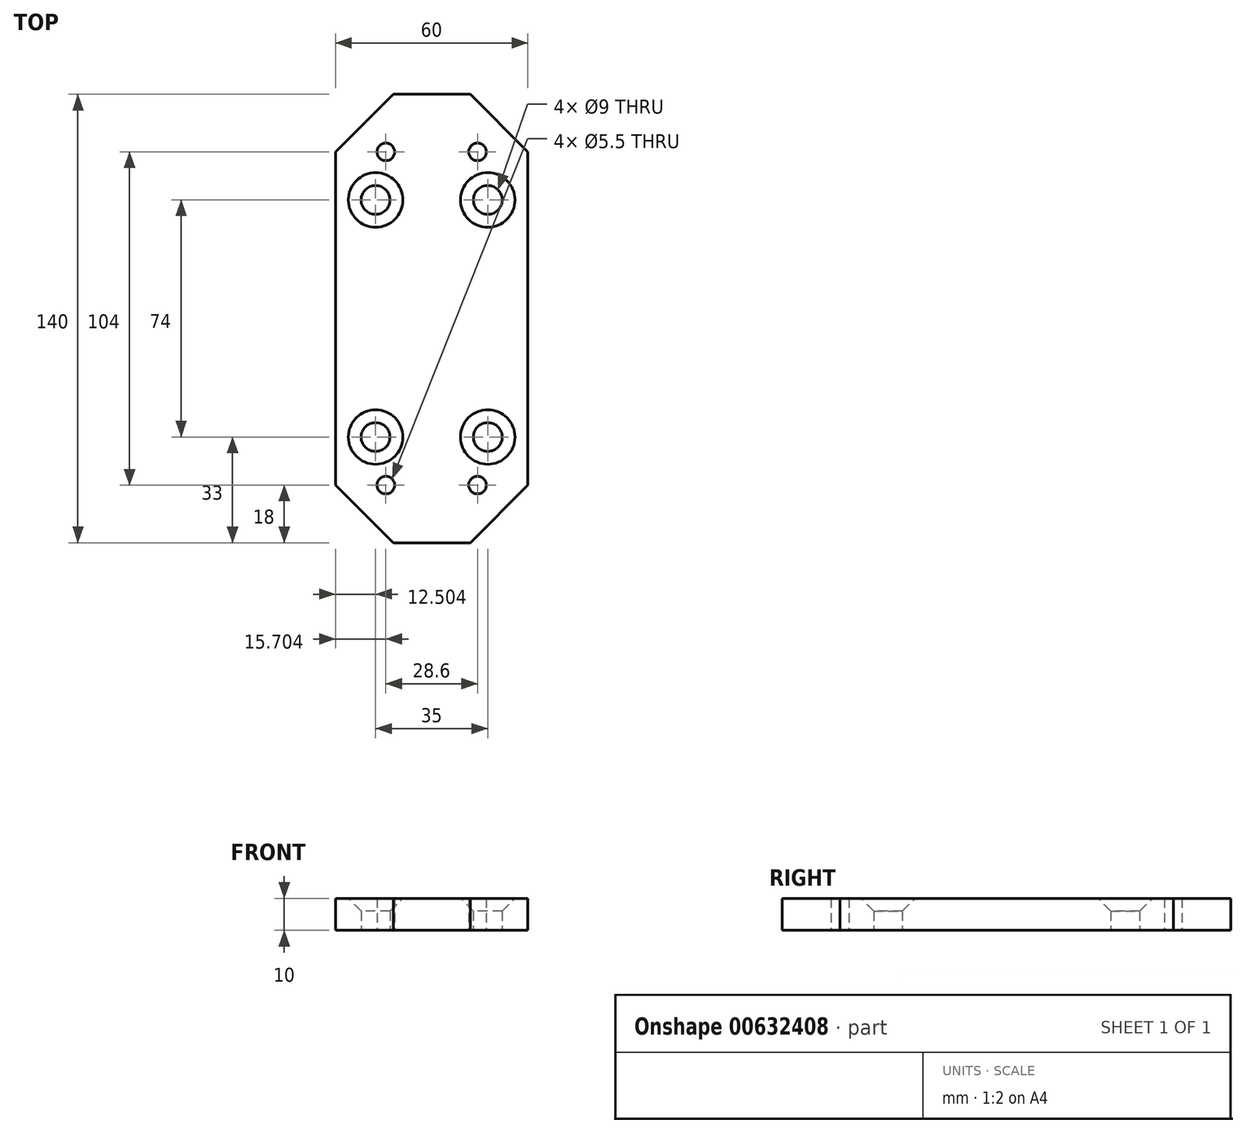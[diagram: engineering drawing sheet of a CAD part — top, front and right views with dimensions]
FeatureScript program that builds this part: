
annotation { "Feature Type Name" : "Feature", "Feature Type Description" : "" }
export const myFeature = defineFeature(function(context is Context, id is Id, definition is map)
    precondition{}
    {
        {
            var Q0;
            Q0=qCreatedBy(makeId("Top.planeOp"),FACE);
            var sketch = newSketch(context, id + "F0", { "sketchPlane" : qUnion([Q0])});
            skLineSegment(sketch, "E0.bottom", {"start": v(27.22, 0) * mm, "end": v(-32.78, 0) * mm});
            skLineSegment(sketch, "E0.top", {"start": v(27.22, 140) * mm, "end": v(-32.78, 140) * mm});
            skLineSegment(sketch, "E0.left", {"start": v(27.22, 0) * mm, "end": v(27.22, 140) * mm});
            skLineSegment(sketch, "E0.right", {"start": v(-32.78, 0) * mm, "end": v(-32.78, 140) * mm});
            skCircle(sketch, "E1", {"center": v(-20.28, 33) * mm, "radius": 4.5 * mm});
            skCircle(sketch, "E2", {"center": v(14.72, 33) * mm, "radius": 4.5 * mm});
            skCircle(sketch, "E3", {"center": v(-20.28, 107) * mm, "radius": 4.5 * mm});
            skCircle(sketch, "E4", {"center": v(14.72, 107) * mm, "radius": 4.5 * mm});
            skCircle(sketch, "E5", {"center": v(-17.08, 18) * mm, "radius": 2.75 * mm});
            skCircle(sketch, "E6", {"center": v(11.52, 18) * mm, "radius": 2.75 * mm});
            skCircle(sketch, "E7", {"center": v(11.52, 122) * mm, "radius": 2.75 * mm});
            skCircle(sketch, "E8", {"center": v(-17.08, 122) * mm, "radius": 2.75 * mm});
            skSolve(sketch);
        }
        {
            var Q0;
            Q0=makeQuery(id+"F0.imprint","IMPRINT",FACE,{"disambiguationData":[TD([[makeQuery(id+"F0.imprint","IMPRINT",EDGE,{"derivedFrom":sQuery(id+"F0.wireOp",EDGE,"E0.bottom")}),-1.0]])]});
            extrude(context, id + "F1", {"entities" : qUnion([Q0]), "depth" : 10 * mm, "offsetDistance" : 25 * mm});
        }
        {
            var Q0;
            Q0=makeQuery(id+"F1.opExtrude","CAP_EDGE",EDGE,{"disambiguationData":[OSD([sQuery(id+"F0.wireOp",EDGE,"E1")])],"isStart":false});
            var Q1;
            Q1=makeQuery(id+"F1.opExtrude","CAP_EDGE",EDGE,{"disambiguationData":[OSD([sQuery(id+"F0.wireOp",EDGE,"E2")])],"isStart":false});
            var Q2;
            Q2=makeQuery(id+"F1.opExtrude","CAP_EDGE",EDGE,{"disambiguationData":[OSD([sQuery(id+"F0.wireOp",EDGE,"E4")])],"isStart":false});
            var Q3;
            Q3=makeQuery(id+"F1.opExtrude","CAP_EDGE",EDGE,{"disambiguationData":[OSD([sQuery(id+"F0.wireOp",EDGE,"E3")])],"isStart":false});
            chamfer(context, id + "F2", {"entities" : qUnion([Q0, Q1, Q2, Q3]), "width" : 4 * mm, "tangentPropagation" : true});
        }
        {
            var Q0;
            Q0=makeQuery(id+"F1.opExtrude","SWEPT_EDGE",EDGE,{"disambiguationData":[OSD([sQuery(id+"F0.wireOp",EDGE,"E0.bottom"),sQuery(id+"F0.wireOp",EDGE,"E0.right")])]});
            var Q1;
            Q1=makeQuery(id+"F1.opExtrude","SWEPT_EDGE",EDGE,{"disambiguationData":[OSD([sQuery(id+"F0.wireOp",EDGE,"E0.bottom"),sQuery(id+"F0.wireOp",EDGE,"E0.left")])]});
            var Q2;
            Q2=makeQuery(id+"F1.opExtrude","SWEPT_EDGE",EDGE,{"disambiguationData":[OSD([sQuery(id+"F0.wireOp",EDGE,"E0.top"),sQuery(id+"F0.wireOp",EDGE,"E0.left")])]});
            var Q3;
            Q3=makeQuery(id+"F1.opExtrude","SWEPT_EDGE",EDGE,{"disambiguationData":[OSD([sQuery(id+"F0.wireOp",EDGE,"E0.top"),sQuery(id+"F0.wireOp",EDGE,"E0.right")])]});
            chamfer(context, id + "F3", {"entities" : qUnion([Q0, Q1, Q2, Q3]), "width" : 18 * mm, "tangentPropagation" : true});
        }
    });
